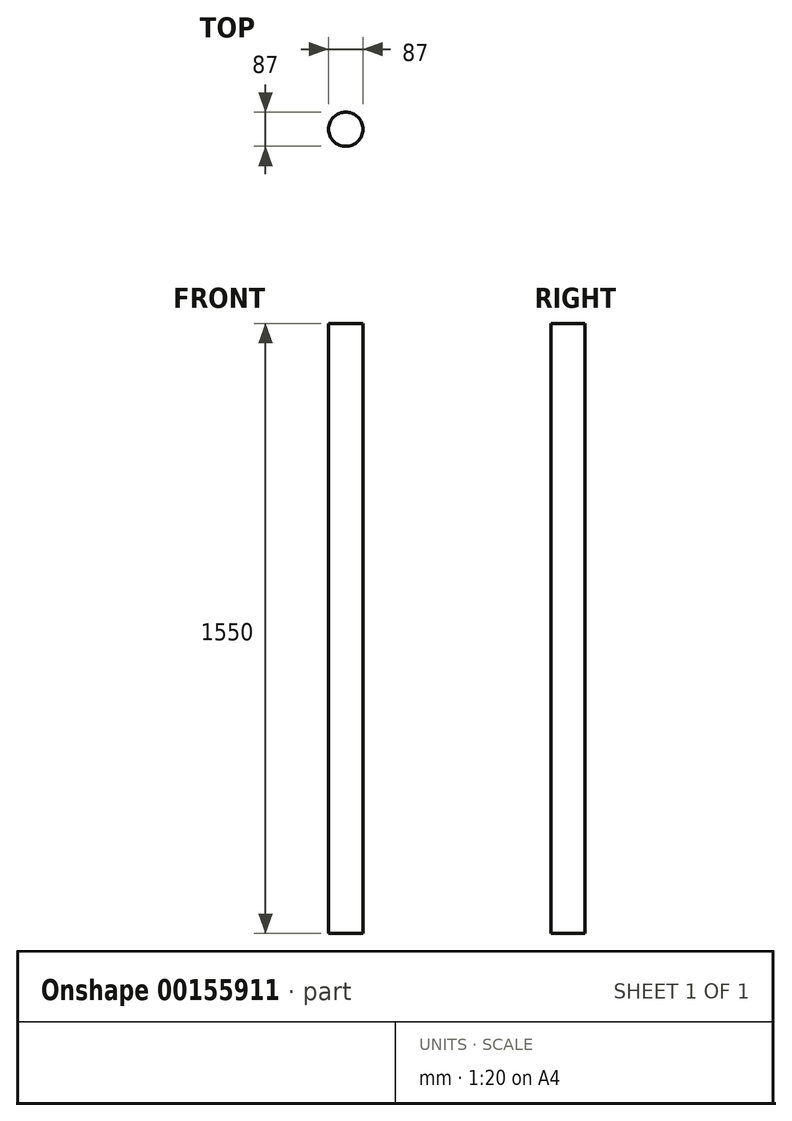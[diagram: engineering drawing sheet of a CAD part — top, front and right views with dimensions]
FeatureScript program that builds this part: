
annotation { "Feature Type Name" : "Feature", "Feature Type Description" : "" }
export const myFeature = defineFeature(function(context is Context, id is Id, definition is map)
    precondition{}
    {
        {
            var Q0;
            Q0=qCreatedBy(makeId("Top.planeOp"),FACE);
            var sketch = newSketch(context, id + "F0", { "sketchPlane" : qUnion([Q0])});
            skCircle(sketch, "E0", {"center": v(0, 0) * mm, "radius": 43.5 * mm});
            skSolve(sketch);
        }
        {
            var Q0;
            Q0 = qSketchRegion(id + "F0", true);
            extrude(context, id + "F1", {"entities" : qUnion([Q0]), "depth" : 1550 * mm});
        }
    });
